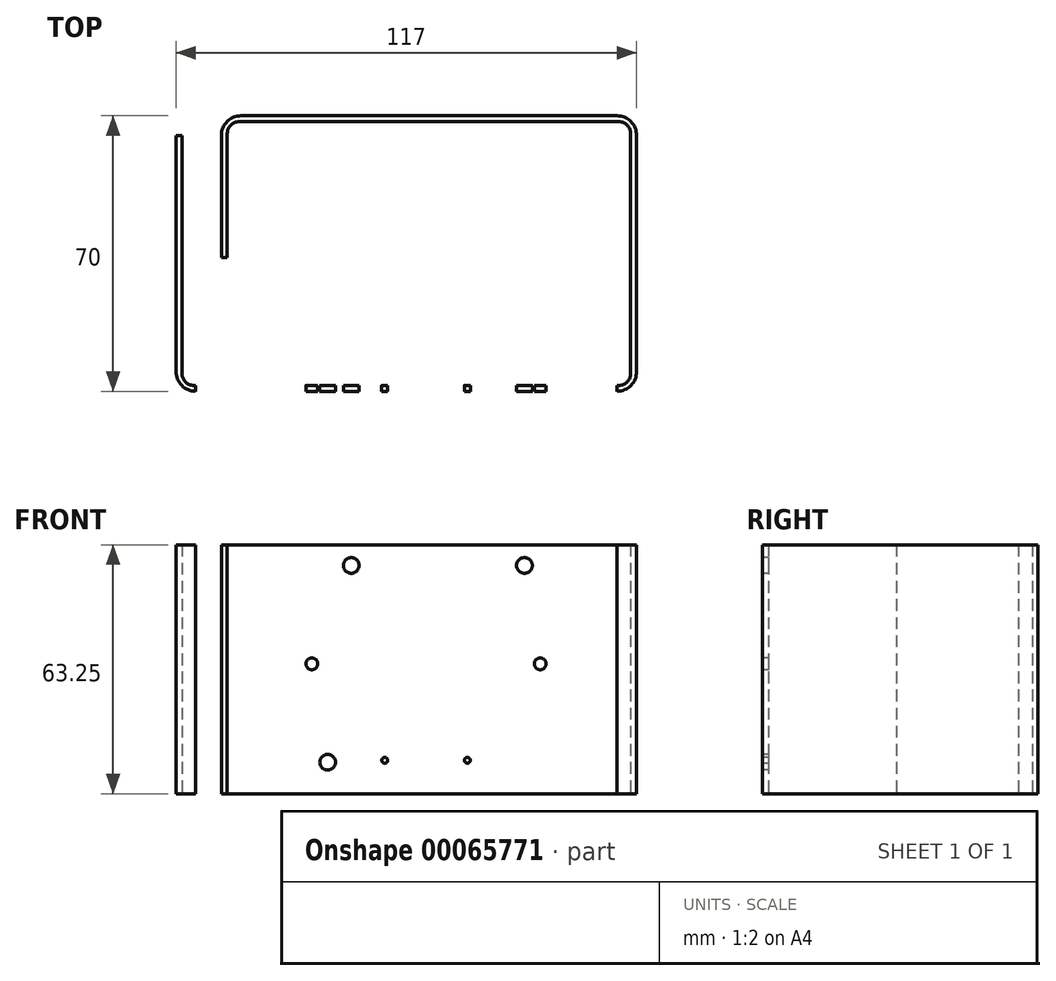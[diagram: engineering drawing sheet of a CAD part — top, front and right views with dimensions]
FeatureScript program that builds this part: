
annotation { "Feature Type Name" : "Feature", "Feature Type Description" : "" }
export const myFeature = defineFeature(function(context is Context, id is Id, definition is map)
    precondition{}
    {
        {
            var Q0;
            Q0=qCreatedBy(makeId("Top.planeOp"),FACE);
            var sketch = newSketch(context, id + "F0", { "sketchPlane" : qUnion([Q0])});
            skLineSegment(sketch, "E0", {"start": v(-62.75, 30) * mm, "end": v(-62.75, -30.5) * mm});
            skLineSegment(sketch, "E1", {"start": v(-59.75, -33.5) * mm, "end": v(48.25, -33.5) * mm});
            skLineSegment(sketch, "E2", {"start": v(51.25, -30.5) * mm, "end": v(51.25, 30.5) * mm});
            skLineSegment(sketch, "E3", {"start": v(48.25, 33.5) * mm, "end": v(-48.25, 33.5) * mm});
            skLineSegment(sketch, "E4", {"start": v(-51.25, 30.5) * mm, "end": v(-51.25, -1) * mm});
            skLineSegment(sketch, "E5.0", {"start": v(-52.75, 30) * mm, "end": v(-52.75, -1) * mm});
            skLineSegment(sketch, "E5.1", {"start": v(-64.25, 30) * mm, "end": v(-64.25, -30) * mm});
            skLineSegment(sketch, "E5.2", {"start": v(-59.25, -35) * mm, "end": v(47.75, -35) * mm});
            skLineSegment(sketch, "E5.3", {"start": v(52.75, -30) * mm, "end": v(52.75, 30) * mm});
            skLineSegment(sketch, "E5.4", {"start": v(47.75, 35) * mm, "end": v(-47.75, 35) * mm});
            skLineSegment(sketch, "E6", {"start": v(-51.25, -1) * mm, "end": v(-52.75, -1) * mm});
            skLineSegment(sketch, "E7", {"start": v(-62.75, 30) * mm, "end": v(-64.25, 30) * mm});
            skPoint(sketch, "E8.visualSharp", {"position": v(-62.75, -33.5) * mm});
            skArc(sketch, "E8.filletArc", {"start": v(-62.75, -30.5) * mm, "mid": v(-61.87, -32.62) * mm, "end": v(-59.75, -33.5) * mm});
            skPoint(sketch, "E9.visualSharp", {"position": v(51.25, -33.5) * mm});
            skArc(sketch, "E9.filletArc", {"start": v(48.25, -33.5) * mm, "mid": v(50.37, -32.62) * mm, "end": v(51.25, -30.5) * mm});
            skPoint(sketch, "E10.visualSharp", {"position": v(51.25, 33.5) * mm});
            skArc(sketch, "E10.filletArc", {"start": v(51.25, 30.5) * mm, "mid": v(50.37, 32.62) * mm, "end": v(48.25, 33.5) * mm});
            skPoint(sketch, "E11.visualSharp", {"position": v(-51.25, 33.5) * mm});
            skArc(sketch, "E11.filletArc", {"start": v(-48.25, 33.5) * mm, "mid": v(-50.37, 32.62) * mm, "end": v(-51.25, 30.5) * mm});
            skPoint(sketch, "E12.visualSharp", {"position": v(-64.25, -35) * mm});
            skArc(sketch, "E12.filletArc", {"start": v(-64.25, -30) * mm, "mid": v(-62.79, -33.54) * mm, "end": v(-59.25, -35) * mm});
            skPoint(sketch, "E13.visualSharp", {"position": v(52.75, -35) * mm});
            skArc(sketch, "E13.filletArc", {"start": v(47.75, -35) * mm, "mid": v(51.29, -33.54) * mm, "end": v(52.75, -30) * mm});
            skPoint(sketch, "E14.visualSharp", {"position": v(52.75, 35) * mm});
            skArc(sketch, "E14.filletArc", {"start": v(52.75, 30) * mm, "mid": v(51.29, 33.54) * mm, "end": v(47.75, 35) * mm});
            skPoint(sketch, "E15.visualSharp", {"position": v(-52.75, 35) * mm});
            skArc(sketch, "E15.filletArc", {"start": v(-47.75, 35) * mm, "mid": v(-51.29, 33.54) * mm, "end": v(-52.75, 30) * mm});
            skLineSegment(sketch, "E16", {"start": v(51.25, 0) * mm, "end": v(-12.48, 0) * mm, "construction": true});
            skLineSegment(sketch, "E17", {"start": v(0, 33.5) * mm, "end": v(0, -15.26) * mm, "construction": true});
            skSolve(sketch);
        }
        {
            var Q0;
            Q0=qSketchRegion(id+"F0",true);
            extrude(context, id + "F1", {"entities" : qUnion([Q0]), "depth" : 63.25 * mm});
        }
        {
            var Q0;
            Q0=makeQuery(id+"F1.opExtrude","SWEPT_FACE",FACE,{"disambiguationData":[OSD([sQuery(id+"F0.wireOp",EDGE,"E5.2")])]});
            var sketch = newSketch(context, id + "F2", { "sketchPlane" : qUnion([Q0])});
            skLineSegment(sketch, "E18.bottom", {"start": v(-22.75, 52) * mm, "end": v(21.25, 52) * mm});
            skLineSegment(sketch, "E18.top", {"start": v(-22.75, 14) * mm, "end": v(21.25, 14) * mm});
            skLineSegment(sketch, "E18.left", {"start": v(-25.75, 49) * mm, "end": v(-25.75, 17) * mm});
            skLineSegment(sketch, "E18.right", {"start": v(24.25, 49) * mm, "end": v(24.25, 17) * mm});
            skLineSegment(sketch, "E19", {"start": v(-59.25, 33) * mm, "end": v(47.75, 33) * mm, "construction": true});
            skLineSegment(sketch, "E20", {"start": v(24.25, 33) * mm, "end": v(-25.75, 33) * mm, "construction": true});
            skLineSegment(sketch, "E21", {"start": v(-0.75, 52) * mm, "end": v(-0.75, 14) * mm, "construction": true});
            skLineSegment(sketch, "E22", {"start": v(-5.75, 63.25) * mm, "end": v(-5.75, 0) * mm, "construction": true});
            skPoint(sketch, "E23.visualSharp", {"position": v(-25.75, 52) * mm});
            skArc(sketch, "E23.filletArc", {"start": v(-22.75, 52) * mm, "mid": v(-24.87, 51.12) * mm, "end": v(-25.75, 49) * mm});
            skPoint(sketch, "E24.visualSharp", {"position": v(24.25, 52) * mm});
            skArc(sketch, "E24.filletArc", {"start": v(24.25, 49) * mm, "mid": v(23.37, 51.12) * mm, "end": v(21.25, 52) * mm});
            skPoint(sketch, "E25.visualSharp", {"position": v(24.25, 14) * mm});
            skArc(sketch, "E25.filletArc", {"start": v(21.25, 14) * mm, "mid": v(23.37, 14.88) * mm, "end": v(24.25, 17) * mm});
            skPoint(sketch, "E26.visualSharp", {"position": v(-25.75, 14) * mm});
            skArc(sketch, "E26.filletArc", {"start": v(-25.75, 17) * mm, "mid": v(-24.87, 14.88) * mm, "end": v(-22.75, 14) * mm});
            skCircle(sketch, "E27", {"center": v(-29.75, 33) * mm, "radius": 1.5 * mm});
            skCircle(sketch, "E28.MirrorC", {"center": v(28.25, 33) * mm, "radius": 1.5 * mm});
            skCircle(sketch, "E29", {"center": v(-25.75, 58) * mm, "radius": 2 * mm});
            skCircle(sketch, "E30.MirrorC", {"center": v(24.25, 58) * mm, "radius": 2 * mm});
            skCircle(sketch, "E31.MirrorC", {"center": v(-25.75, 8) * mm, "radius": 2 * mm});
            skCircle(sketch, "E32.MirrorC", {"center": v(24.25, 8) * mm, "radius": 2 * mm});
            skLineSegment(sketch, "E33.bottom", {"start": v(-6.75, 7) * mm, "end": v(5.25, 7) * mm});
            skPoint(sketch, "E34.visualSharp", {"position": v(6.75, 10) * mm});
            skLineSegment(sketch, "E33.top", {"start": v(-6.75, 10) * mm, "end": v(5.25, 10) * mm});
            skArc(sketch, "E35.filletArc", {"start": v(-6.75, 10) * mm, "mid": v(-7.81, 9.56) * mm, "end": v(-8.25, 8.5) * mm});
            skLineSegment(sketch, "E33.left", {"start": v(-8.25, 8.5) * mm, "end": v(-8.25, 8.5) * mm});
            skLineSegment(sketch, "E33.right", {"start": v(6.75, 8.5) * mm, "end": v(6.75, 8.5) * mm});
            skArc(sketch, "E36.filletArc", {"start": v(-8.25, 8.5) * mm, "mid": v(-7.81, 7.44) * mm, "end": v(-6.75, 7) * mm});
            skArc(sketch, "E37.filletArc", {"start": v(5.25, 7) * mm, "mid": v(6.31, 7.44) * mm, "end": v(6.75, 8.5) * mm});
            skArc(sketch, "E34.filletArc", {"start": v(6.75, 8.5) * mm, "mid": v(6.31, 9.56) * mm, "end": v(5.25, 10) * mm});
            skCircle(sketch, "E38", {"center": v(-11.25, 8.5) * mm, "radius": 0.75 * mm});
            skPoint(sketch, "E39", {"position": v(-0.75, 10) * mm});
            skLineSegment(sketch, "E40", {"start": v(-11.25, 8.5) * mm, "end": v(7.39, 8.5) * mm, "construction": true});
            skPoint(sketch, "E35.visualSharp", {"position": v(-8.25, 10) * mm});
            skPoint(sketch, "E36.visualSharp", {"position": v(-8.25, 7) * mm});
            skPoint(sketch, "E37.visualSharp", {"position": v(6.75, 7) * mm});
            skLineSegment(sketch, "E41", {"start": v(-0.75, 10) * mm, "end": v(-0.75, 7) * mm, "construction": true});
            skCircle(sketch, "E42.MirrorC", {"center": v(9.75, 8.5) * mm, "radius": 0.75 * mm});
            skLineSegment(sketch, "E43", {"start": v(-25.75, 8) * mm, "end": v(-25.75, 58) * mm, "construction": true});
            skLineSegment(sketch, "E44", {"start": v(24.25, 58) * mm, "end": v(24.25, 8) * mm, "construction": true});
            skLineSegment(sketch, "E45", {"start": v(-25.75, 8) * mm, "end": v(24.25, 8) * mm, "construction": true});
            skLineSegment(sketch, "E46", {"start": v(24.25, 58) * mm, "end": v(-25.75, 58) * mm, "construction": true});
            skCircle(sketch, "E47", {"center": v(-19.75, 8) * mm, "radius": 2 * mm});
            skCircle(sketch, "E48.MirrorC", {"center": v(-19.75, 58) * mm, "radius": 2 * mm});
            skCircle(sketch, "E49.MirrorC", {"center": v(18.25, 58) * mm, "radius": 2 * mm});
            skCircle(sketch, "E50", {"center": v(15.25, 8) * mm, "radius": 2 * mm});
            skPoint(sketch, "E51", {"position": v(-59.25, 31.62) * mm});
            skSolve(sketch);
        }
        {
            var Q0;
            Q0=makeQuery(id+"F2.imprint","IMPRINT",FACE,{"disambiguationData":[TD([[makeQuery(id+"F2.imprint","IMPRINT",EDGE,{"derivedFrom":sQuery(id+"F2.wireOp",EDGE,"E18.bottom")}),-1.0]])]});
            var Q1;
            Q1=makeQuery(id+"F2.imprint","IMPRINT",FACE,{"disambiguationData":[TD([[makeQuery(id+"F2.imprint","IMPRINT",EDGE,{"derivedFrom":sQuery(id+"F2.wireOp",EDGE,"5223969e-9384-4705-a09f-08a9d0864926")}),1.0]])]});
            var Q2;
            Q2=makeQuery(id+"F2.imprint","IMPRINT",FACE,{"disambiguationData":[TD([[makeQuery(id+"F2.imprint","IMPRINT",EDGE,{"derivedFrom":sQuery(id+"F2.wireOp",EDGE,"b6238159-0034-45e9-8c88-9dabcd8353630.MirrorC")}),-1.0]])]});
            var Q3;
            Q3=makeQuery(id+"F2.imprint","IMPRINT",FACE,{"disambiguationData":[TD([[makeQuery(id+"F2.imprint","IMPRINT",EDGE,{"derivedFrom":sQuery(id+"F2.wireOp",EDGE,"E29")}),1.0]])]});
            var Q4;
            Q4=makeQuery(id+"F2.imprint","IMPRINT",FACE,{"disambiguationData":[TD([[makeQuery(id+"F2.imprint","IMPRINT",EDGE,{"derivedFrom":sQuery(id+"F2.wireOp",EDGE,"E30.MirrorC")}),-1.0]])]});
            var Q5;
            Q5=makeQuery(id+"F2.imprint","IMPRINT",FACE,{"disambiguationData":[TD([[makeQuery(id+"F2.imprint","IMPRINT",EDGE,{"derivedFrom":sQuery(id+"F2.wireOp",EDGE,"E32.MirrorC")}),1.0]])]});
            var Q6;
            Q6=makeQuery(id+"F2.imprint","IMPRINT",FACE,{"disambiguationData":[TD([[makeQuery(id+"F2.imprint","IMPRINT",EDGE,{"derivedFrom":sQuery(id+"F2.wireOp",EDGE,"E31.MirrorC")}),-1.0]])]});
            var Q7;
            Q7=makeQuery(id+"F2.imprint","IMPRINT",FACE,{"disambiguationData":[TD([[makeQuery(id+"F2.imprint","IMPRINT",EDGE,{"derivedFrom":sQuery(id+"F2.wireOp",EDGE,"E33.bottom")}),1.0]])]});
            var Q8;
            Q8=makeQuery(id+"F2.imprint","IMPRINT",FACE,{"disambiguationData":[TD([[makeQuery(id+"F2.imprint","IMPRINT",EDGE,{"derivedFrom":sQuery(id+"F2.wireOp",EDGE,"E47")}),1.0]])]});
            var Q9;
            Q9=makeQuery(id+"F2.imprint","IMPRINT",FACE,{"disambiguationData":[TD([[makeQuery(id+"F2.imprint","IMPRINT",EDGE,{"derivedFrom":sQuery(id+"F2.wireOp",EDGE,"E48.MirrorC")}),-1.0]])]});
            var Q10;
            Q10=makeQuery(id+"F2.imprint","IMPRINT",FACE,{"disambiguationData":[TD([[makeQuery(id+"F2.imprint","IMPRINT",EDGE,{"derivedFrom":sQuery(id+"F2.wireOp",EDGE,"E49.MirrorC")}),1.0]])]});
            var Q11;
            Q11=makeQuery(id+"F2.imprint","IMPRINT",FACE,{"disambiguationData":[TD([[makeQuery(id+"F2.imprint","IMPRINT",EDGE,{"derivedFrom":sQuery(id+"F2.wireOp",EDGE,"E50")}),1.0]])]});
            extrude(context, id + "F3", {"entities" : qUnion([Q0, Q1, Q2, Q3, Q4, Q5, Q6, Q7, Q8, Q9, Q10, Q11]), "operationType" : NewBodyOperationType.REMOVE, "oppositeDirection" : true, "depth" : 25 * mm});
        }
    });
